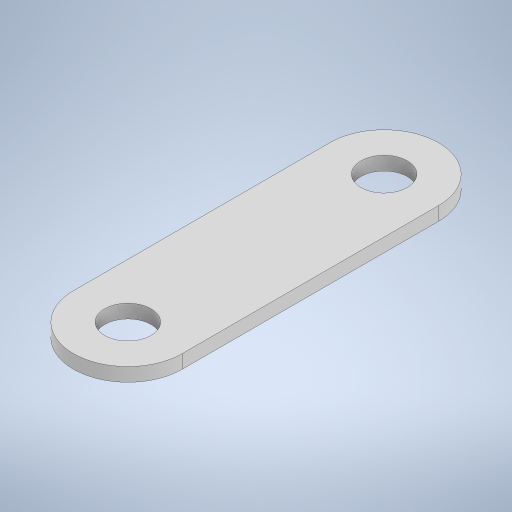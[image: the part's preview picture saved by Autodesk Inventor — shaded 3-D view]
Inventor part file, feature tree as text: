
AUTODESK INVENTOR PART (.ipt)
format: ipt  version: 2024.1 (Build 281209000, 209)  size: 229,888 bytes
history: native  units: mm
features: other x1, extrude x1, sketch x1
ambient origin geometry x8: Origin, YZ Plane, XZ Plane, XY Plane, X Axis, Y Axis, Z Axis, Center Point
bodies: Body1 (feature_tree)
feature tree (3):
  other  "ソリッド1"
  extrude  "押し出し1"  Depth=47.1mm
  sketch  "スケッチ1"
